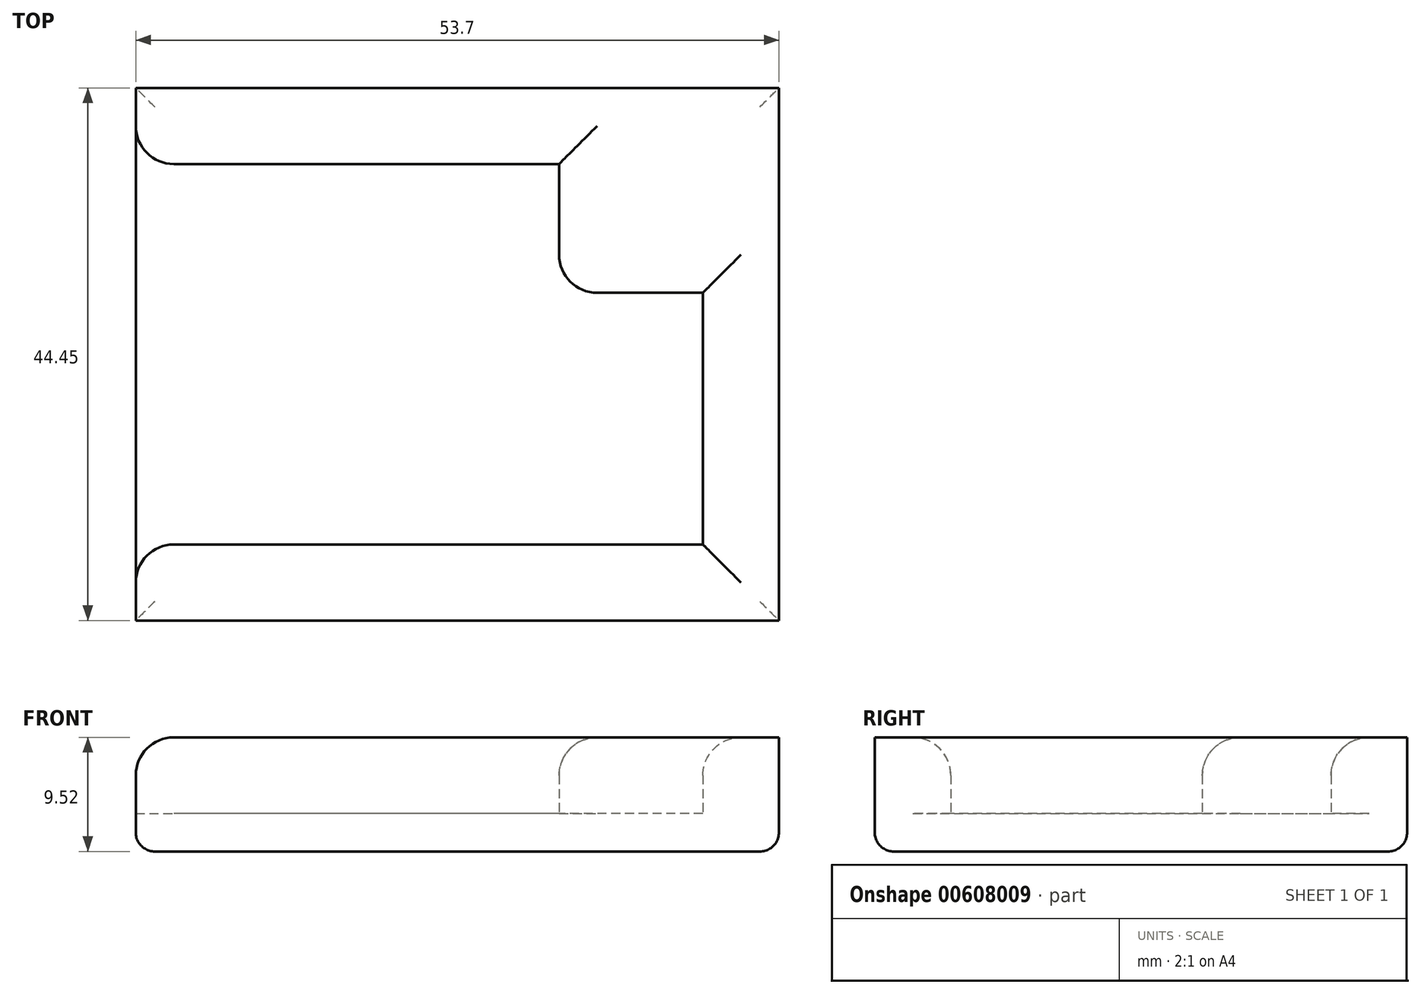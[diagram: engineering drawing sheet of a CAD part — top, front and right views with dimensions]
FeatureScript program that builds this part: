
annotation { "Feature Type Name" : "Feature", "Feature Type Description" : "" }
export const myFeature = defineFeature(function(context is Context, id is Id, definition is map)
    precondition{}
    {
        {
            var Q0;
            Q0=qCreatedBy(makeId("Top.planeOp"),FACE);
            var sketch = newSketch(context, id + "F0", { "sketchPlane" : qUnion([Q0])});
            skLineSegment(sketch, "E0.bottom", {"start": v(20.5, 10.5) * mm, "end": v(8.5, 10.5) * mm});
            skLineSegment(sketch, "E0.top", {"start": v(20.5, -10.5) * mm, "end": v(-20.5, -10.5) * mm});
            skLineSegment(sketch, "E0.left", {"start": v(20.5, 10.5) * mm, "end": v(20.5, -10.5) * mm});
            skLineSegment(sketch, "E0.right", {"start": v(-20.5, 10.5) * mm, "end": v(-20.5, -10.5) * mm});
            skPoint(sketch, "E0.middle", {"position": v(0, 0) * mm});
            skLineSegment(sketch, "E1.top", {"start": v(-20.5, 21.25) * mm, "end": v(8.5, 21.25) * mm});
            skLineSegment(sketch, "E1.left", {"start": v(-20.5, 10.5) * mm, "end": v(-20.5, 21.25) * mm});
            skLineSegment(sketch, "E1.right", {"start": v(8.5, 10.5) * mm, "end": v(8.5, 21.25) * mm});
            skLineSegment(sketch, "E2.bottom", {"start": v(-26.85, -16.85) * mm, "end": v(26.85, -16.85) * mm});
            skLineSegment(sketch, "E2.top", {"start": v(-26.85, 27.6) * mm, "end": v(26.85, 27.6) * mm});
            skLineSegment(sketch, "E2.left", {"start": v(-26.85, -16.85) * mm, "end": v(-26.85, 27.6) * mm});
            skLineSegment(sketch, "E2.right", {"start": v(26.85, -16.85) * mm, "end": v(26.85, 27.6) * mm});
            skLineSegment(sketch, "E3", {"start": v(-20.5, 21.25) * mm, "end": v(-26.85, 21.25) * mm});
            skLineSegment(sketch, "E4", {"start": v(-20.5, -10.5) * mm, "end": v(-26.85, -10.5) * mm});
            skSolve(sketch);
        }
        {
            var Q0;
            Q0=makeQuery(id+"F0.imprint","IMPRINT",FACE,{"disambiguationData":[TD([[makeQuery(id+"F0.imprint","IMPRINT",EDGE,{"derivedFrom":sQuery(id+"F0.wireOp",EDGE,"E0.bottom")}),-1.0]])]});
            var Q1;
            Q1=makeQuery(id+"F0.imprint","IMPRINT",FACE,{"disambiguationData":[TD([[makeQuery(id+"F0.imprint","IMPRINT",EDGE,{"derivedFrom":sQuery(id+"F0.wireOp",EDGE,"E0.bottom")}),1.0]])]});
            var Q2;
            Q2=makeQuery(id+"F0.imprint","IMPRINT",FACE,{"disambiguationData":[TD([[makeQuery(id+"F0.imprint","IMPRINT",EDGE,{"derivedFrom":sQuery(id+"F0.wireOp",EDGE,"E0.right")}),-1.0]])]});
            extrude(context, id + "F1", {"entities" : qUnion([Q0, Q1, Q2]), "oppositeDirection" : true, "depth" : 3.17 * mm, "offsetDistance" : 25.4 * mm});
        }
        {
            var Q0;
            Q0=makeQuery(id+"F0.imprint","IMPRINT",FACE,{"disambiguationData":[TD([[makeQuery(id+"F0.imprint","IMPRINT",EDGE,{"derivedFrom":sQuery(id+"F0.wireOp",EDGE,"E0.bottom")}),-1.0]])]});
            extrude(context, id + "F2", {"entities" : qUnion([Q0]), "operationType" : NewBodyOperationType.ADD, "depth" : 6.35 * mm, "offsetDistance" : 25.4 * mm});
        }
        {
            var Q0;
            Q0=makeQuery(id+"F2.opExtrude","SWEPT_EDGE",EDGE,{"disambiguationData":[OSD([sQuery(id+"F0.wireOp",EDGE,"E0.bottom"),sQuery(id+"F0.wireOp",EDGE,"E1.right")])]});
            var Q1;
            Q1=makeQuery(id+"F2.opExtrude","SWEPT_EDGE",EDGE,{"disambiguationData":[OSD([sQuery(id+"F0.wireOp",EDGE,"E2.left"),sQuery(id+"F0.wireOp",EDGE,"E4")])]});
            var Q2;
            Q2=makeQuery(id+"F2.opExtrude","SWEPT_EDGE",EDGE,{"disambiguationData":[OSD([sQuery(id+"F0.wireOp",EDGE,"E2.left"),sQuery(id+"F0.wireOp",EDGE,"E3")])]});
            fillet(context, id + "F3", {"entities" : qUnion([Q0, Q1, Q2]), "radius" : 3.17 * mm, "tangentPropagation" : true, "allowEdgeOverflow" : false});
        }
        {
            var Q0;
            {var subQ0=sQuery(id+"F0.wireOp",EDGE,"E1.right");var subQ1=sQuery(id+"F0.wireOp",EDGE,"E0.bottom");Q0=makeQuery(id+"F3.opFillet","BLEND_EDGE",EDGE,{"blendedFrom":[makeQuery(id+"F2.opExtrude","SWEPT_EDGE",EDGE,{"disambiguationData":[OSD([subQ1,subQ0])]}),makeQuery(id+"F2.opExtrude","CAP_FACE",FACE,{"disambiguationData":[OSD([subQ1,sQuery(id+"F0.wireOp",EDGE,"E0.top"),sQuery(id+"F0.wireOp",EDGE,"E0.left"),sQuery(id+"F0.wireOp",EDGE,"E1.top"),subQ0,sQuery(id+"F0.wireOp",EDGE,"E2.bottom"),sQuery(id+"F0.wireOp",EDGE,"E2.top"),sQuery(id+"F0.wireOp",EDGE,"E2.left"),sQuery(id+"F0.wireOp",EDGE,"E2.right"),sQuery(id+"F0.wireOp",EDGE,"E3"),sQuery(id+"F0.wireOp",EDGE,"E4")])],"isStart":false})],"blendedInto":[makeQuery(id+"F2.opExtrude","CAP_FACE",FACE,{"disambiguationData":[OSD([subQ1,sQuery(id+"F0.wireOp",EDGE,"E0.top"),sQuery(id+"F0.wireOp",EDGE,"E0.left"),sQuery(id+"F0.wireOp",EDGE,"E1.top"),subQ0,sQuery(id+"F0.wireOp",EDGE,"E2.bottom"),sQuery(id+"F0.wireOp",EDGE,"E2.top"),sQuery(id+"F0.wireOp",EDGE,"E2.left"),sQuery(id+"F0.wireOp",EDGE,"E2.right"),sQuery(id+"F0.wireOp",EDGE,"E3"),sQuery(id+"F0.wireOp",EDGE,"E4")])],"isStart":false})]});}
            var Q1;
            Q1=makeQuery(id+"F2.opExtrude","CAP_EDGE",EDGE,{"disambiguationData":[OSD([sQuery(id+"F0.wireOp",EDGE,"E0.left")])],"isStart":false});
            var Q2;
            Q2=makeQuery(id+"F2.opExtrude","CAP_EDGE",EDGE,{"disambiguationData":[OSD([sQuery(id+"F0.wireOp",EDGE,"E0.top"),sQuery(id+"F0.wireOp",EDGE,"E4")])],"isStart":false});
            var Q3;
            Q3=makeQuery(id+"F2.opExtrude","CAP_EDGE",EDGE,{"disambiguationData":[OSD([sQuery(id+"F0.wireOp",EDGE,"E1.top"),sQuery(id+"F0.wireOp",EDGE,"E3")])],"isStart":false});
            fillet(context, id + "F4", {"entities" : qUnion([Q0, Q1, Q2, Q3]), "radius" : 3.17 * mm, "tangentPropagation" : true, "allowEdgeOverflow" : false});
        }
        {
            var Q0;
            Q0=makeQuery(id+"F1.opExtrude","CAP_FACE",FACE,{"disambiguationData":[OSD([sQuery(id+"F0.wireOp",EDGE,"E2.bottom"),sQuery(id+"F0.wireOp",EDGE,"E2.top"),sQuery(id+"F0.wireOp",EDGE,"E2.left"),sQuery(id+"F0.wireOp",EDGE,"E2.right")])],"isStart":false});
            fillet(context, id + "F5", {"entities" : qUnion([Q0]), "radius" : 1.59 * mm, "tangentPropagation" : true, "allowEdgeOverflow" : false});
        }
    });
